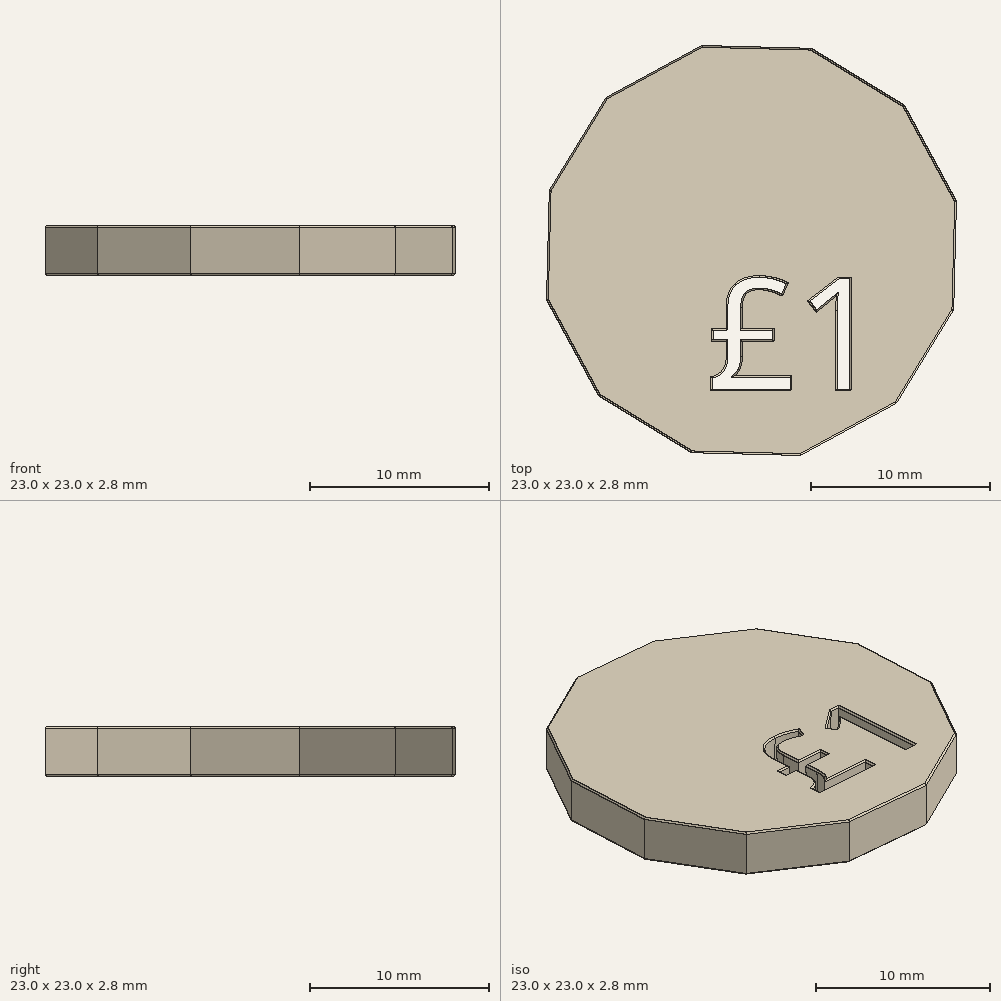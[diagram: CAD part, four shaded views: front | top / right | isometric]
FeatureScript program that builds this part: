
annotation { "Feature Type Name" : "Feature", "Feature Type Description" : "" }
export const myFeature = defineFeature(function(context is Context, id is Id, definition is map)
    precondition{}
    {
        {
            var Q0;
            Q0=qCreatedBy(makeId("Top.planeOp"),FACE);
            var sketch = newSketch(context, id + "F0", { "sketchPlane" : qUnion([Q0])});
            skCircle(sketch, "E0.cCircle", {"center": v(0, 0) * mm, "radius": 11.83 * mm, "construction": true});
            skLineSegment(sketch, "E0.0", {"start": v(11.34, -3.35) * mm, "end": v(8.15, -8.58) * mm});
            skLineSegment(sketch, "E0.1", {"start": v(8.15, -8.58) * mm, "end": v(2.77, -11.5) * mm});
            skLineSegment(sketch, "E0.2", {"start": v(2.77, -11.5) * mm, "end": v(-3.35, -11.34) * mm});
            skLineSegment(sketch, "E0.3", {"start": v(-3.35, -11.34) * mm, "end": v(-8.58, -8.15) * mm});
            skLineSegment(sketch, "E0.4", {"start": v(-8.58, -8.15) * mm, "end": v(-11.5, -2.77) * mm});
            skLineSegment(sketch, "E0.5", {"start": v(-11.5, -2.77) * mm, "end": v(-11.34, 3.35) * mm});
            skLineSegment(sketch, "E0.6", {"start": v(-11.34, 3.35) * mm, "end": v(-8.15, 8.58) * mm});
            skLineSegment(sketch, "E0.7", {"start": v(-8.15, 8.58) * mm, "end": v(-2.77, 11.5) * mm});
            skLineSegment(sketch, "E0.8", {"start": v(-2.77, 11.5) * mm, "end": v(3.35, 11.34) * mm});
            skLineSegment(sketch, "E0.9", {"start": v(3.35, 11.34) * mm, "end": v(8.58, 8.15) * mm});
            skLineSegment(sketch, "E0.10", {"start": v(8.58, 8.15) * mm, "end": v(11.5, 2.77) * mm});
            skLineSegment(sketch, "E0.11", {"start": v(11.5, 2.77) * mm, "end": v(11.34, -3.35) * mm});
            skSolve(sketch);
        }
        {
            var Q0;
            Q0=makeQuery(id+"F0.imprint","IMPRINT",FACE,{"disambiguationData":[TD([[makeQuery(id+"F0.imprint","IMPRINT",EDGE,{"derivedFrom":sQuery(id+"F0.wireOp",EDGE,"E0.0")}),-1.0]])]});
            extrude(context, id + "F1", {"entities" : qUnion([Q0]), "depth" : 2.8 * mm, "offsetDistance" : 25 * mm});
        }
        {
            var Q0;
            Q0=makeQuery(id+"F1.opExtrude","CAP_FACE",FACE,{"disambiguationData":[OSD([sQuery(id+"F0.wireOp",EDGE,"E0.0"),sQuery(id+"F0.wireOp",EDGE,"E0.1"),sQuery(id+"F0.wireOp",EDGE,"E0.2"),sQuery(id+"F0.wireOp",EDGE,"E0.3"),sQuery(id+"F0.wireOp",EDGE,"E0.4"),sQuery(id+"F0.wireOp",EDGE,"E0.5"),sQuery(id+"F0.wireOp",EDGE,"E0.6"),sQuery(id+"F0.wireOp",EDGE,"E0.7"),sQuery(id+"F0.wireOp",EDGE,"E0.8"),sQuery(id+"F0.wireOp",EDGE,"E0.9"),sQuery(id+"F0.wireOp",EDGE,"E0.10"),sQuery(id+"F0.wireOp",EDGE,"E0.11")])],"isStart":false});
            var sketch = newSketch(context, id + "F2", { "sketchPlane" : qUnion([Q0])});
            skText(sketch, "E1", { "text": "£1", "fontName": "OpenSans-Regular.ttf"});
            skPoint(sketch, "E1.firstSnap0", {"position": v(5.96, 9.74) * mm});
            const initialGuessF2  = {"E1": [-0.00245, -0.00777, 1, 0, 0.00623]};
            skSetInitialGuess(sketch, initialGuessF2);
            skSolve(sketch);
        }
        {
            var Q0;
            Q0=makeQuery(id+"F2.imprint","IMPRINT",FACE,{"disambiguationData":[TD([[makeQuery(id+"F2.imprint","IMPRINT",EDGE,{"derivedFrom":sQuery(id+"F2.wireOp",EDGE,"E1.sketch_text.stroke-0")}),-1.0]])]});
            var Q1;
            Q1=makeQuery(id+"F2.imprint","IMPRINT",FACE,{"disambiguationData":[TD([[makeQuery(id+"F2.imprint","IMPRINT",EDGE,{"derivedFrom":sQuery(id+"F2.wireOp",EDGE,"E1.sketch_text.stroke-24")}),-1.0]])]});
            extrude(context, id + "F3", {"entities" : qUnion([Q0, Q1]), "operationType" : NewBodyOperationType.REMOVE, "oppositeDirection" : true, "depth" : 3 * mm, "offsetDistance" : 25 * mm, "hasDraft" : true, "draftAngle" : 3 * degree});
        }
        {
            var Q0;
            Q0=makeQuery(id+"F1.opExtrude","CAP_FACE",FACE,{"disambiguationData":[OSD([sQuery(id+"F0.wireOp",EDGE,"E0.0"),sQuery(id+"F0.wireOp",EDGE,"E0.1"),sQuery(id+"F0.wireOp",EDGE,"E0.2"),sQuery(id+"F0.wireOp",EDGE,"E0.3"),sQuery(id+"F0.wireOp",EDGE,"E0.4"),sQuery(id+"F0.wireOp",EDGE,"E0.5"),sQuery(id+"F0.wireOp",EDGE,"E0.6"),sQuery(id+"F0.wireOp",EDGE,"E0.7"),sQuery(id+"F0.wireOp",EDGE,"E0.8"),sQuery(id+"F0.wireOp",EDGE,"E0.9"),sQuery(id+"F0.wireOp",EDGE,"E0.10"),sQuery(id+"F0.wireOp",EDGE,"E0.11")])],"isStart":false});
            var Q1;
            Q1=makeQuery(id+"F1.opExtrude","CAP_FACE",FACE,{"disambiguationData":[OSD([sQuery(id+"F0.wireOp",EDGE,"E0.0"),sQuery(id+"F0.wireOp",EDGE,"E0.1"),sQuery(id+"F0.wireOp",EDGE,"E0.2"),sQuery(id+"F0.wireOp",EDGE,"E0.3"),sQuery(id+"F0.wireOp",EDGE,"E0.4"),sQuery(id+"F0.wireOp",EDGE,"E0.5"),sQuery(id+"F0.wireOp",EDGE,"E0.6"),sQuery(id+"F0.wireOp",EDGE,"E0.7"),sQuery(id+"F0.wireOp",EDGE,"E0.8"),sQuery(id+"F0.wireOp",EDGE,"E0.9"),sQuery(id+"F0.wireOp",EDGE,"E0.10"),sQuery(id+"F0.wireOp",EDGE,"E0.11")])],"isStart":true});
            chamfer(context, id + "F4", {"entities" : qUnion([Q0, Q1]), "width" : 0.1 * mm, "tangentPropagation" : true});
        }
    });
